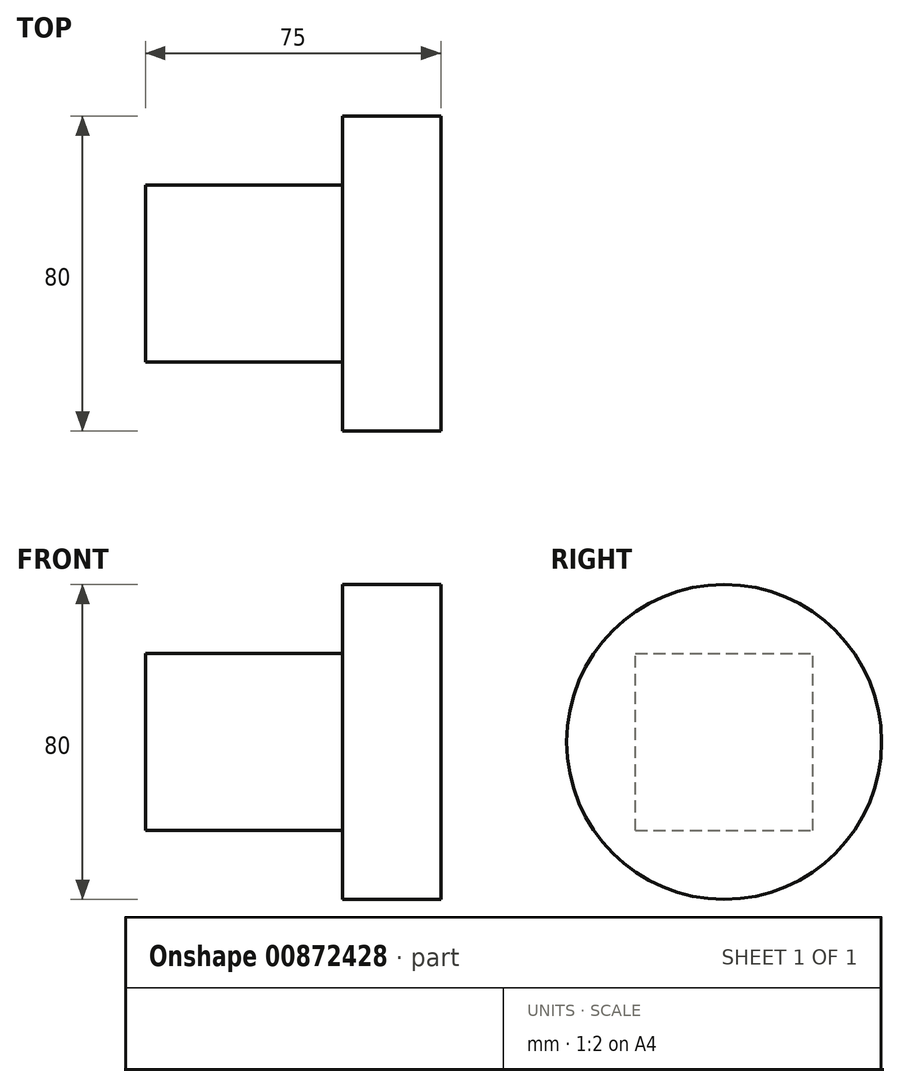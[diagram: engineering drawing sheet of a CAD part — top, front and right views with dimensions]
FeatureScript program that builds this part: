
annotation { "Feature Type Name" : "Feature", "Feature Type Description" : "" }
export const myFeature = defineFeature(function(context is Context, id is Id, definition is map)
    precondition{}
    {
        {
            var Q0;
            Q0=qCreatedBy(makeId("Right.planeOp"),FACE);
            cPlane(context, id + "F0", {"entities" : qUnion([Q0]), "cplaneType" : CPlaneType.OFFSET, "offset" : 100 * mm, "width" : 150 * mm, "height" : 150 * mm});
        }
        {
            var Q0;
            Q0=qCreatedBy(id+"F0.planeOp",FACE);
            var sketch = newSketch(context, id + "F1", { "sketchPlane" : qUnion([Q0])});
            skCircle(sketch, "E0", {"center": v(0, 0) * mm, "radius": 40 * mm});
            skSolve(sketch);
        }
        {
            var Q0;
            Q0=makeQuery(id+"F1.imprint","IMPRINT",FACE,{"disambiguationData":[TD([[makeQuery(id+"F1.imprint","IMPRINT",EDGE,{"derivedFrom":sQuery(id+"F1.wireOp",EDGE,"E0")}),1.0]])]});
            extrude(context, id + "F2", {"entities" : qUnion([Q0]), "depth" : 25 * mm, "offsetDistance" : 25 * mm});
        }
        {
            var Q0;
            Q0=makeQuery(id+"F2.opExtrude","CAP_FACE",FACE,{"disambiguationData":[OSD([sQuery(id+"F1.wireOp",EDGE,"E0")])],"isStart":true});
            var sketch = newSketch(context, id + "F3", { "sketchPlane" : qUnion([Q0])});
            skLineSegment(sketch, "E1.bottom", {"start": v(22.5, -22.5) * mm, "end": v(-22.5, -22.5) * mm});
            skLineSegment(sketch, "E1.top", {"start": v(22.5, 22.5) * mm, "end": v(-22.5, 22.5) * mm});
            skLineSegment(sketch, "E1.left", {"start": v(22.5, -22.5) * mm, "end": v(22.5, 22.5) * mm});
            skLineSegment(sketch, "E1.right", {"start": v(-22.5, -22.5) * mm, "end": v(-22.5, 22.5) * mm});
            skPoint(sketch, "E1.middle", {"position": v(0, 0) * mm});
            skSolve(sketch);
        }
        {
            var Q0;
            Q0=makeQuery(id+"F3.imprint","IMPRINT",FACE,{"disambiguationData":[TD([[makeQuery(id+"F3.imprint","IMPRINT",EDGE,{"derivedFrom":sQuery(id+"F3.wireOp",EDGE,"E1.bottom")}),-1.0]])]});
            extrude(context, id + "F4", {"entities" : qUnion([Q0]), "operationType" : NewBodyOperationType.ADD, "depth" : 50 * mm, "offsetDistance" : 25 * mm});
        }
    });
